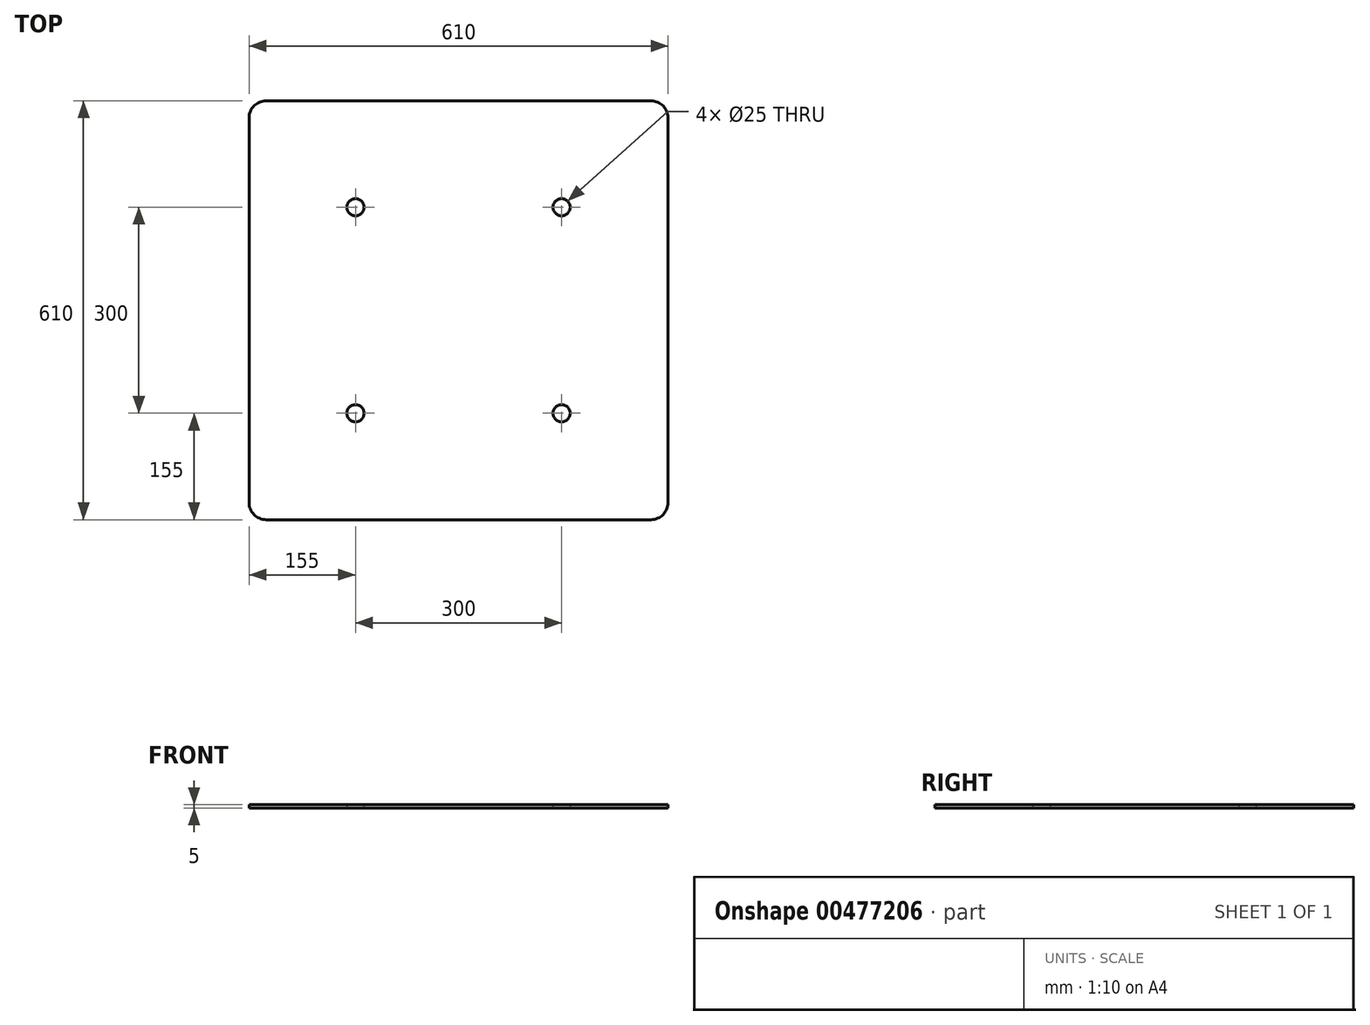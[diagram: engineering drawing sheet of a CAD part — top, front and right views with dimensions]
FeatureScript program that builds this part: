
annotation { "Feature Type Name" : "Feature", "Feature Type Description" : "" }
export const myFeature = defineFeature(function(context is Context, id is Id, definition is map)
    precondition{}
    {
        {
            var Q0;
            Q0=qCreatedBy(makeId("Top.planeOp"),FACE);
            var sketch = newSketch(context, id + "F0", { "sketchPlane" : qUnion([Q0])});
            skLineSegment(sketch, "E0.bottom", {"start": v(25, 0) * mm, "end": v(585, 0) * mm});
            skLineSegment(sketch, "E0.top", {"start": v(25, 610) * mm, "end": v(585, 610) * mm});
            skLineSegment(sketch, "E0.left", {"start": v(0, 25) * mm, "end": v(0, 585) * mm});
            skLineSegment(sketch, "E0.right", {"start": v(610, 25) * mm, "end": v(610, 585) * mm});
            skPoint(sketch, "E1.visualSharp", {"position": v(0, 610) * mm});
            skArc(sketch, "E1.filletArc", {"start": v(25, 610) * mm, "mid": v(7.32, 602.68) * mm, "end": v(0, 585) * mm});
            skPoint(sketch, "E2.visualSharp", {"position": v(0, 0) * mm});
            skArc(sketch, "E2.filletArc", {"start": v(0, 25) * mm, "mid": v(7.32, 7.32) * mm, "end": v(25, 0) * mm});
            skPoint(sketch, "E3.visualSharp", {"position": v(610, 0) * mm});
            skArc(sketch, "E3.filletArc", {"start": v(585, 0) * mm, "mid": v(602.68, 7.32) * mm, "end": v(610, 25) * mm});
            skPoint(sketch, "E4.visualSharp", {"position": v(610, 610) * mm});
            skArc(sketch, "E4.filletArc", {"start": v(610, 585) * mm, "mid": v(602.68, 602.68) * mm, "end": v(585, 610) * mm});
            skCircle(sketch, "E5", {"center": v(155, 155) * mm, "radius": 12.5 * mm});
            skLineSegment(sketch, "E6", {"start": v(305, 610) * mm, "end": v(305, 0) * mm, "construction": true});
            skLineSegment(sketch, "E7", {"start": v(0, 305) * mm, "end": v(610, 305) * mm, "construction": true});
            skCircle(sketch, "E8.0.1.0", {"center": v(155, 455) * mm, "radius": 12.5 * mm});
            skCircle(sketch, "E8.1.0.0", {"center": v(455, 155) * mm, "radius": 12.5 * mm});
            skCircle(sketch, "E8.1.1.0", {"center": v(455, 455) * mm, "radius": 12.5 * mm});
            skLineSegment(sketch, "E8.direction1", {"start": v(155, 155) * mm, "end": v(455, 155) * mm, "construction": true});
            skLineSegment(sketch, "E8.direction2", {"start": v(155, 155) * mm, "end": v(155, 455) * mm, "construction": true});
            skSolve(sketch);
        }
        {
            var Q0;
            Q0=makeQuery(id+"F0.imprint","IMPRINT",FACE,{"disambiguationData":[TD([[makeQuery(id+"F0.imprint","IMPRINT",EDGE,{"derivedFrom":sQuery(id+"F0.wireOp",EDGE,"E0.bottom")}),1.0]])]});
            extrude(context, id + "F1", {"entities" : qUnion([Q0]), "depth" : 5 * mm});
        }
    });
